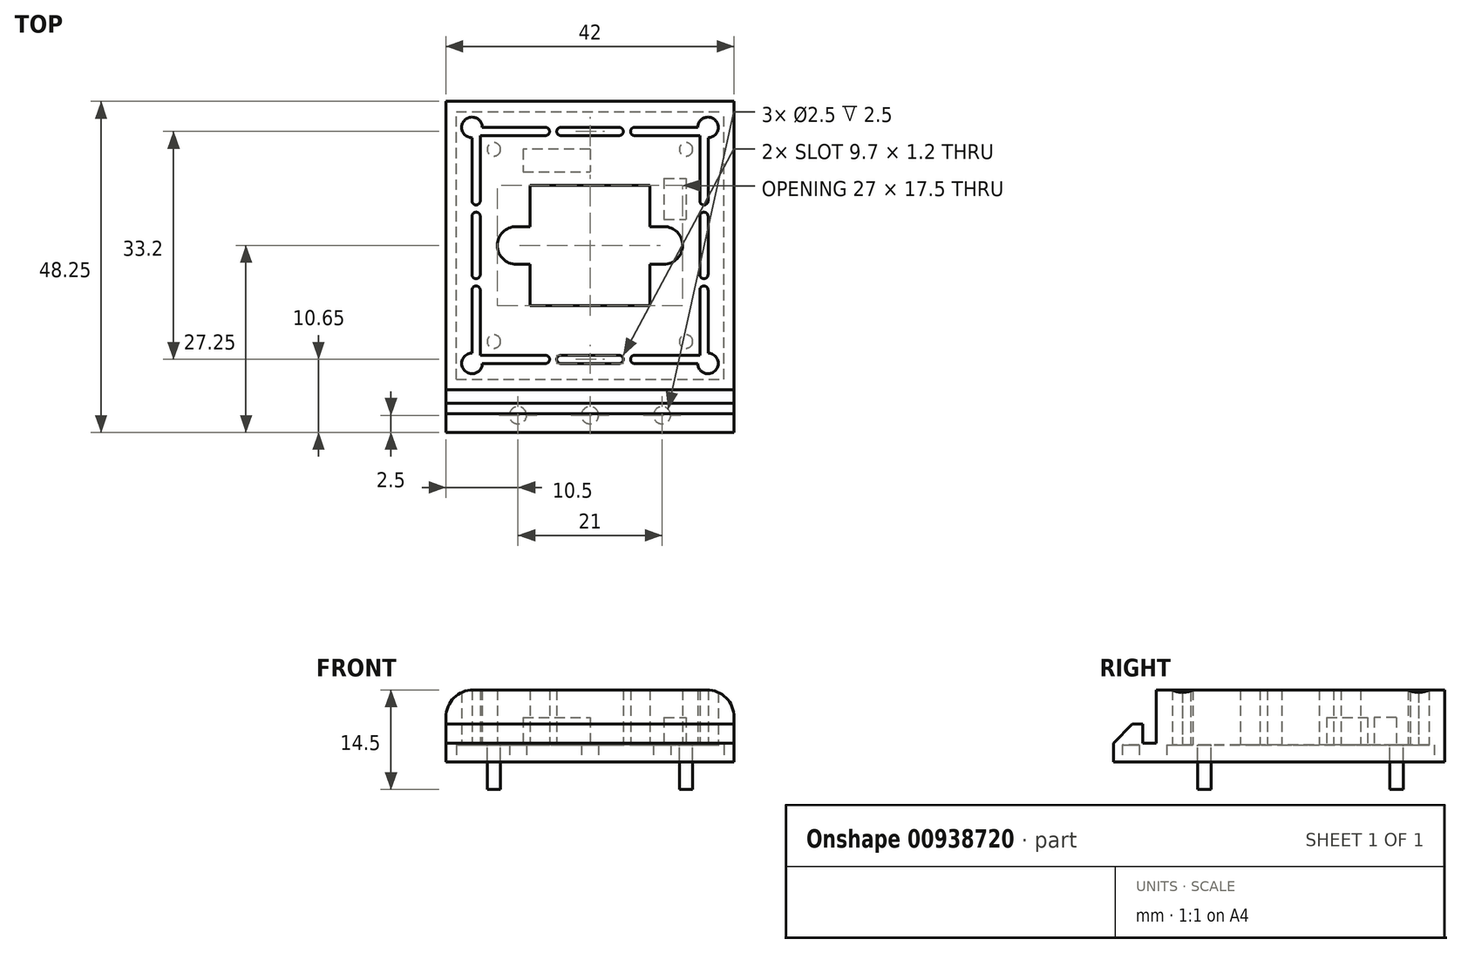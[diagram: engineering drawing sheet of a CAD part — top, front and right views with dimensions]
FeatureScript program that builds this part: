
annotation { "Feature Type Name" : "Feature", "Feature Type Description" : "" }
export const myFeature = defineFeature(function(context is Context, id is Id, definition is map)
    precondition{}
    {
        {
            var Q0;
            Q0=qCreatedBy(makeId("Top.planeOp"),FACE);
            var sketch = newSketch(context, id + "F0", { "sketchPlane" : qUnion([Q0])});
            skLineSegment(sketch, "E0.bottom", {"start": v(19, 19) * mm, "end": v(-19, 19) * mm, "construction": true});
            skLineSegment(sketch, "E0.top", {"start": v(19, -19) * mm, "end": v(-19, -19) * mm, "construction": true});
            skLineSegment(sketch, "E0.left", {"start": v(19, 19) * mm, "end": v(19, -19) * mm, "construction": true});
            skLineSegment(sketch, "E0.right", {"start": v(-19, 19) * mm, "end": v(-19, -19) * mm, "construction": true});
            skPoint(sketch, "E0.middle", {"position": v(0, 0) * mm});
            skPoint(sketch, "E1", {"position": v(19, 0) * mm});
            skPoint(sketch, "E2", {"position": v(-19, 0) * mm});
            skPoint(sketch, "E3", {"position": v(0, 19) * mm});
            skPoint(sketch, "E4", {"position": v(0, -19) * mm});
            skPoint(sketch, "E5", {"position": v(17.2, 0) * mm});
            skPoint(sketch, "E6", {"position": v(-17.2, 0) * mm});
            skLineSegment(sketch, "E7", {"start": v(-19, 0) * mm, "end": v(-17.2, 0) * mm, "construction": true});
            skLineSegment(sketch, "E8", {"start": v(19, 0) * mm, "end": v(17.2, 0) * mm, "construction": true});
            skLineSegment(sketch, "E9", {"start": v(0, 19) * mm, "end": v(0, 17.2) * mm, "construction": true});
            skLineSegment(sketch, "E10", {"start": v(0, -17.2) * mm, "end": v(0, -19) * mm, "construction": true});
            skPoint(sketch, "E11", {"position": v(-16, 16) * mm});
            skPoint(sketch, "E12", {"position": v(16, -16) * mm});
            skPoint(sketch, "E13", {"position": v(16, 16) * mm});
            skPoint(sketch, "E14", {"position": v(-16, -16) * mm});
            skPoint(sketch, "E15", {"position": v(17.2, 4.25) * mm});
            skPoint(sketch, "E16", {"position": v(17.2, -4.25) * mm});
            skPoint(sketch, "E17", {"position": v(16, -4.25) * mm});
            skPoint(sketch, "E18", {"position": v(16, 4.25) * mm});
            skPoint(sketch, "E19", {"position": v(-17.2, 4.25) * mm});
            skPoint(sketch, "E20", {"position": v(-16, 4.25) * mm});
            skPoint(sketch, "E21", {"position": v(-17.2, -4.25) * mm});
            skPoint(sketch, "E22", {"position": v(-16, -4.25) * mm});
            skPoint(sketch, "E23", {"position": v(-4.25, 17.2) * mm});
            skPoint(sketch, "E24", {"position": v(-4.25, 16) * mm});
            skPoint(sketch, "E25", {"position": v(4.25, 17.2) * mm});
            skPoint(sketch, "E26", {"position": v(4.25, 16) * mm});
            skPoint(sketch, "E27", {"position": v(-4.25, -16) * mm});
            skPoint(sketch, "E28", {"position": v(4.25, -16) * mm});
            skPoint(sketch, "E29", {"position": v(-4.25, -17.2) * mm});
            skPoint(sketch, "E30", {"position": v(4.25, -17.2) * mm});
            skLineSegment(sketch, "E31", {"start": v(17.2, 4.25) * mm, "end": v(17.2, -4.25) * mm});
            skLineSegment(sketch, "E32", {"start": v(16, 4.25) * mm, "end": v(16, -4.25) * mm});
            skLineSegment(sketch, "E33", {"start": v(4.25, 16) * mm, "end": v(-4.25, 16) * mm});
            skLineSegment(sketch, "E34", {"start": v(-4.25, 17.2) * mm, "end": v(4.25, 17.2) * mm});
            skLineSegment(sketch, "E35", {"start": v(-16, 4.25) * mm, "end": v(-16, -4.25) * mm});
            skLineSegment(sketch, "E36", {"start": v(-17.2, -4.25) * mm, "end": v(-17.2, 4.25) * mm});
            skLineSegment(sketch, "E37", {"start": v(-4.25, -16) * mm, "end": v(4.25, -16) * mm});
            skLineSegment(sketch, "E38", {"start": v(4.25, -17.2) * mm, "end": v(-4.25, -17.2) * mm});
            skArc(sketch, "E39", {"start": v(16, 4.25) * mm, "mid": v(16.6, 4.85) * mm, "end": v(17.2, 4.25) * mm});
            skArc(sketch, "E40", {"start": v(17.2, -4.25) * mm, "mid": v(16.6, -4.85) * mm, "end": v(16, -4.25) * mm});
            skArc(sketch, "E41", {"start": v(4.25, -16) * mm, "mid": v(4.85, -16.6) * mm, "end": v(4.25, -17.2) * mm});
            skArc(sketch, "E42", {"start": v(-4.25, -16) * mm, "mid": v(-4.85, -16.6) * mm, "end": v(-4.25, -17.2) * mm});
            skArc(sketch, "E43", {"start": v(-17.2, -4.25) * mm, "mid": v(-16.6, -4.85) * mm, "end": v(-16, -4.25) * mm});
            skArc(sketch, "E44", {"start": v(-17.2, 4.25) * mm, "mid": v(-16.6, 4.85) * mm, "end": v(-16, 4.25) * mm});
            skArc(sketch, "E45", {"start": v(-4.25, 16) * mm, "mid": v(-4.85, 16.6) * mm, "end": v(-4.25, 17.2) * mm});
            skArc(sketch, "E46", {"start": v(4.25, 16) * mm, "mid": v(4.85, 16.6) * mm, "end": v(4.25, 17.2) * mm});
            skPoint(sketch, "E47", {"position": v(-6.5, 16) * mm});
            skPoint(sketch, "E48", {"position": v(-6.5, 17.2) * mm});
            skPoint(sketch, "E49", {"position": v(-16, 6.5) * mm});
            skPoint(sketch, "E50", {"position": v(-17.2, 6.5) * mm});
            skPoint(sketch, "E51", {"position": v(6.5, 16) * mm});
            skPoint(sketch, "E52", {"position": v(6.5, 17.2) * mm});
            skPoint(sketch, "E53", {"position": v(16, 6.5) * mm});
            skPoint(sketch, "E54", {"position": v(17.2, 6.5) * mm});
            skPoint(sketch, "E55", {"position": v(-17.2, -6.5) * mm});
            skPoint(sketch, "E56", {"position": v(-16, -6.5) * mm});
            skPoint(sketch, "E57", {"position": v(17.2, -6.5) * mm});
            skPoint(sketch, "E58", {"position": v(16, -6.5) * mm});
            skPoint(sketch, "E59", {"position": v(6.5, -17.2) * mm});
            skPoint(sketch, "E60", {"position": v(6.5, -16) * mm});
            skPoint(sketch, "E61", {"position": v(-6.5, -17.2) * mm});
            skPoint(sketch, "E62", {"position": v(-6.5, -16) * mm});
            skLineSegment(sketch, "E63", {"start": v(-6.5, 17.2) * mm, "end": v(-6.5, 16) * mm, "construction": true});
            skLineSegment(sketch, "E64", {"start": v(-17.2, 6.5) * mm, "end": v(-16, 6.5) * mm, "construction": true});
            skLineSegment(sketch, "E65", {"start": v(6.5, 17.2) * mm, "end": v(6.5, 16) * mm, "construction": true});
            skLineSegment(sketch, "E66", {"start": v(16, 6.5) * mm, "end": v(17.2, 6.5) * mm, "construction": true});
            skLineSegment(sketch, "E67", {"start": v(-17.2, -6.5) * mm, "end": v(-16, -6.5) * mm, "construction": true});
            skLineSegment(sketch, "E68", {"start": v(-6.5, -16) * mm, "end": v(-6.5, -17.2) * mm, "construction": true});
            skLineSegment(sketch, "E69", {"start": v(16, -6.5) * mm, "end": v(17.2, -6.5) * mm, "construction": true});
            skLineSegment(sketch, "E70", {"start": v(6.5, -16) * mm, "end": v(6.5, -17.2) * mm, "construction": true});
            skArc(sketch, "E71", {"start": v(-6.5, 17.2) * mm, "mid": v(-5.9, 16.6) * mm, "end": v(-6.5, 16) * mm});
            skArc(sketch, "E72", {"start": v(-16, 6.5) * mm, "mid": v(-16.6, 5.9) * mm, "end": v(-17.2, 6.5) * mm});
            skArc(sketch, "E73", {"start": v(6.5, 17.2) * mm, "mid": v(5.9, 16.6) * mm, "end": v(6.5, 16) * mm});
            skArc(sketch, "E74", {"start": v(17.2, 6.5) * mm, "mid": v(16.6, 5.9) * mm, "end": v(16, 6.5) * mm});
            skArc(sketch, "E75", {"start": v(-16, -6.5) * mm, "mid": v(-16.6, -5.9) * mm, "end": v(-17.2, -6.5) * mm});
            skArc(sketch, "E76", {"start": v(-6.5, -16) * mm, "mid": v(-5.9, -16.6) * mm, "end": v(-6.5, -17.2) * mm});
            skArc(sketch, "E77", {"start": v(6.5, -16) * mm, "mid": v(5.9, -16.6) * mm, "end": v(6.5, -17.2) * mm});
            skArc(sketch, "E78", {"start": v(17.2, -6.5) * mm, "mid": v(16.6, -5.9) * mm, "end": v(16, -6.5) * mm});
            skLineSegment(sketch, "E79", {"start": v(6.5, 17.2) * mm, "end": v(16, 17.2) * mm});
            skLineSegment(sketch, "E80", {"start": v(6.5, 16) * mm, "end": v(16, 16) * mm});
            skLineSegment(sketch, "E81", {"start": v(16, 6.5) * mm, "end": v(16, 16) * mm});
            skLineSegment(sketch, "E82", {"start": v(17.2, 16) * mm, "end": v(17.2, 6.5) * mm});
            skLineSegment(sketch, "E83", {"start": v(-16, 17.2) * mm, "end": v(-6.5, 17.2) * mm});
            skLineSegment(sketch, "E84", {"start": v(-16, 16) * mm, "end": v(-6.5, 16) * mm});
            skLineSegment(sketch, "E85", {"start": v(-16, 16) * mm, "end": v(-16, 6.5) * mm});
            skLineSegment(sketch, "E86", {"start": v(-17.2, 6.5) * mm, "end": v(-17.2, 16) * mm});
            skLineSegment(sketch, "E87", {"start": v(-16, -6.5) * mm, "end": v(-16, -16) * mm});
            skLineSegment(sketch, "E88", {"start": v(-6.5, -16) * mm, "end": v(-16, -16) * mm});
            skLineSegment(sketch, "E89", {"start": v(-17.2, -6.5) * mm, "end": v(-17.2, -16) * mm});
            skLineSegment(sketch, "E90", {"start": v(-16, -17.2) * mm, "end": v(-6.5, -17.2) * mm});
            skLineSegment(sketch, "E91", {"start": v(6.5, -17.2) * mm, "end": v(16, -17.2) * mm});
            skLineSegment(sketch, "E92", {"start": v(6.5, -16) * mm, "end": v(16, -16) * mm});
            skLineSegment(sketch, "E93", {"start": v(17.2, -16) * mm, "end": v(17.2, -6.5) * mm});
            skLineSegment(sketch, "E94", {"start": v(16, -6.5) * mm, "end": v(16, -16) * mm});
            skLineSegment(sketch, "E95", {"start": v(-17.2, 6.5) * mm, "end": v(-19, 6.5) * mm, "construction": true});
            skLineSegment(sketch, "E96", {"start": v(-17.2, -6.5) * mm, "end": v(-19, -6.5) * mm, "construction": true});
            skLineSegment(sketch, "E97", {"start": v(-6.5, 17.2) * mm, "end": v(-6.5, 19) * mm, "construction": true});
            skLineSegment(sketch, "E98", {"start": v(-6.5, -17.2) * mm, "end": v(-6.5, -19) * mm, "construction": true});
            skLineSegment(sketch, "E99", {"start": v(6.5, -17.2) * mm, "end": v(6.5, -19) * mm, "construction": true});
            skLineSegment(sketch, "E100", {"start": v(17.2, -6.5) * mm, "end": v(19, -6.5) * mm, "construction": true});
            skLineSegment(sketch, "E101", {"start": v(17.2, 6.5) * mm, "end": v(19, 6.5) * mm, "construction": true});
            skLineSegment(sketch, "E102", {"start": v(6.5, 17.2) * mm, "end": v(6.5, 19) * mm, "construction": true});
            skPoint(sketch, "E103", {"position": v(-11.25, 17.2) * mm});
            skPoint(sketch, "E104", {"position": v(-11.25, 16) * mm});
            skPoint(sketch, "E105", {"position": v(-17.2, 11.25) * mm});
            skPoint(sketch, "E106", {"position": v(-16, 11.25) * mm});
            skPoint(sketch, "E107", {"position": v(11.25, 17.2) * mm});
            skPoint(sketch, "E108", {"position": v(11.25, 16) * mm});
            skPoint(sketch, "E109", {"position": v(16, 11.25) * mm});
            skPoint(sketch, "E110", {"position": v(17.2, 11.25) * mm});
            skPoint(sketch, "E111", {"position": v(16, -11.25) * mm});
            skPoint(sketch, "E112", {"position": v(17.2, -11.25) * mm});
            skPoint(sketch, "E113", {"position": v(11.25, -16) * mm});
            skPoint(sketch, "E114", {"position": v(11.25, -17.2) * mm});
            skPoint(sketch, "E115", {"position": v(-11.25, -16) * mm});
            skPoint(sketch, "E116", {"position": v(-11.25, -17.2) * mm});
            skPoint(sketch, "E117", {"position": v(-16, -11.25) * mm});
            skPoint(sketch, "E118", {"position": v(-17.2, -11.25) * mm});
            skLineSegment(sketch, "E119", {"start": v(-17.2, 11.25) * mm, "end": v(-16, 11.25) * mm, "construction": true});
            skLineSegment(sketch, "E120", {"start": v(-11.25, 17.2) * mm, "end": v(-11.25, 16) * mm, "construction": true});
            skLineSegment(sketch, "E121", {"start": v(-11.25, -16) * mm, "end": v(-11.25, -17.2) * mm, "construction": true});
            skLineSegment(sketch, "E122", {"start": v(-16, -11.25) * mm, "end": v(-17.2, -11.25) * mm, "construction": true});
            skLineSegment(sketch, "E123", {"start": v(11.25, 17.2) * mm, "end": v(11.25, 16) * mm, "construction": true});
            skLineSegment(sketch, "E124", {"start": v(16, 11.25) * mm, "end": v(17.2, 11.25) * mm, "construction": true});
            skLineSegment(sketch, "E125", {"start": v(11.25, -17.2) * mm, "end": v(11.25, -16) * mm, "construction": true});
            skLineSegment(sketch, "E126", {"start": v(16, -11.25) * mm, "end": v(17.2, -11.25) * mm, "construction": true});
            skPoint(sketch, "E127", {"position": v(-14, 14) * mm});
            skLineSegment(sketch, "E128", {"start": v(-14, 19) * mm, "end": v(-14, 14) * mm, "construction": true});
            skLineSegment(sketch, "E129", {"start": v(-14, 14) * mm, "end": v(-19, 14) * mm, "construction": true});
            skPoint(sketch, "E130", {"position": v(-14, -14) * mm});
            skLineSegment(sketch, "E131", {"start": v(-19, -14) * mm, "end": v(-14, -14) * mm, "construction": true});
            skLineSegment(sketch, "E132", {"start": v(-14, -19) * mm, "end": v(-14, -14) * mm, "construction": true});
            skPoint(sketch, "E133", {"position": v(14, -14) * mm});
            skLineSegment(sketch, "E134", {"start": v(14, -19) * mm, "end": v(14, -14) * mm, "construction": true});
            skLineSegment(sketch, "E135", {"start": v(14, -14) * mm, "end": v(19, -14) * mm, "construction": true});
            skPoint(sketch, "E136", {"position": v(14, 14) * mm});
            skLineSegment(sketch, "E137", {"start": v(14, 19) * mm, "end": v(14, 14) * mm, "construction": true});
            skLineSegment(sketch, "E138", {"start": v(19, 14) * mm, "end": v(14, 14) * mm, "construction": true});
            skPoint(sketch, "E139", {"position": v(16, 0) * mm});
            skPoint(sketch, "E140", {"position": v(0, 16) * mm});
            skPoint(sketch, "E141", {"position": v(-16, 0) * mm});
            skPoint(sketch, "E142", {"position": v(0, -16) * mm});
            skLineSegment(sketch, "E143", {"start": v(16, 0) * mm, "end": v(17.2, 0) * mm, "construction": true});
            skLineSegment(sketch, "E144", {"start": v(0, 17.2) * mm, "end": v(0, 16) * mm, "construction": true});
            skLineSegment(sketch, "E145", {"start": v(0, -16) * mm, "end": v(0, -17.2) * mm, "construction": true});
            skLineSegment(sketch, "E146", {"start": v(-17.2, 0) * mm, "end": v(-16, 0) * mm, "construction": true});
            skPoint(sketch, "E147", {"position": v(-17.2, 17.2) * mm});
            skPoint(sketch, "E148", {"position": v(17.2, 17.2) * mm});
            skPoint(sketch, "E149", {"position": v(-17.2, -17.2) * mm});
            skPoint(sketch, "E150", {"position": v(17.2, -17.2) * mm});
            skLineSegment(sketch, "E151", {"start": v(16, 4.25) * mm, "end": v(17.2, 4.25) * mm, "construction": true});
            skLineSegment(sketch, "E152", {"start": v(16, -4.25) * mm, "end": v(17.2, -4.25) * mm, "construction": true});
            skLineSegment(sketch, "E153", {"start": v(-4.25, 16) * mm, "end": v(-4.25, 17.2) * mm, "construction": true});
            skLineSegment(sketch, "E154", {"start": v(4.25, 16) * mm, "end": v(4.25, 17.2) * mm, "construction": true});
            skLineSegment(sketch, "E155", {"start": v(-16, 4.25) * mm, "end": v(-17.2, 4.25) * mm, "construction": true});
            skLineSegment(sketch, "E156", {"start": v(-16, -4.25) * mm, "end": v(-17.2, -4.25) * mm, "construction": true});
            skLineSegment(sketch, "E157", {"start": v(-4.25, -16) * mm, "end": v(-4.25, -17.2) * mm, "construction": true});
            skLineSegment(sketch, "E158", {"start": v(4.25, -16) * mm, "end": v(4.25, -17.2) * mm, "construction": true});
            skLineSegment(sketch, "E159", {"start": v(-6.5, 17.2) * mm, "end": v(-4.25, 17.2) * mm, "construction": true});
            skLineSegment(sketch, "E160", {"start": v(4.25, 17.2) * mm, "end": v(6.5, 17.2) * mm, "construction": true});
            skLineSegment(sketch, "E161", {"start": v(17.2, 6.5) * mm, "end": v(17.2, 4.25) * mm, "construction": true});
            skLineSegment(sketch, "E162", {"start": v(17.2, -6.5) * mm, "end": v(17.2, -4.25) * mm, "construction": true});
            skLineSegment(sketch, "E163", {"start": v(6.5, -17.2) * mm, "end": v(4.25, -17.2) * mm, "construction": true});
            skLineSegment(sketch, "E164", {"start": v(-4.25, -17.2) * mm, "end": v(-6.5, -17.2) * mm, "construction": true});
            skLineSegment(sketch, "E165", {"start": v(-17.2, -6.5) * mm, "end": v(-17.2, -4.25) * mm, "construction": true});
            skLineSegment(sketch, "E166", {"start": v(-17.2, 4.25) * mm, "end": v(-17.2, 6.5) * mm, "construction": true});
            skCircle(sketch, "E167", {"center": v(14, 14) * mm, "radius": 0.97 * mm});
            skPoint(sketch, "E168", {"position": v(14, 14.97) * mm});
            skPoint(sketch, "E169", {"position": v(14.97, 14) * mm});
            skPoint(sketch, "E170", {"position": v(16, 14) * mm});
            skPoint(sketch, "E171", {"position": v(14, 16) * mm});
            skCircle(sketch, "E172", {"center": v(-14, 14) * mm, "radius": 0.97 * mm});
            skPoint(sketch, "E173", {"position": v(-14, 14.97) * mm});
            skPoint(sketch, "E174", {"position": v(-14.97, 14) * mm});
            skCircle(sketch, "E175", {"center": v(-14, -14) * mm, "radius": 0.97 * mm});
            skCircle(sketch, "E176", {"center": v(14, -14) * mm, "radius": 0.97 * mm});
            skPoint(sketch, "E177", {"position": v(14, -14.97) * mm});
            skPoint(sketch, "E178", {"position": v(14.97, -14) * mm});
            skPoint(sketch, "E179", {"position": v(-14.97, -14) * mm});
            skPoint(sketch, "E180", {"position": v(-14, -14.97) * mm});
            skLineSegment(sketch, "E181.bottom", {"start": v(8.75, 8.75) * mm, "end": v(-8.75, 8.75) * mm});
            skLineSegment(sketch, "E181.top", {"start": v(8.75, -8.75) * mm, "end": v(-8.75, -8.75) * mm});
            skLineSegment(sketch, "E181.left", {"start": v(8.75, 8.75) * mm, "end": v(8.75, 2.75) * mm});
            skLineSegment(sketch, "E181.right", {"start": v(-8.75, 8.75) * mm, "end": v(-8.75, 2.75) * mm});
            skLineSegment(sketch, "E182.bottom", {"start": v(-21, 21) * mm, "end": v(-2.62, 21) * mm});
            skLineSegment(sketch, "E182.top", {"start": v(-21, -21) * mm, "end": v(-2.63, -21) * mm});
            skLineSegment(sketch, "E182.left", {"start": v(-21, 21) * mm, "end": v(-21, -21) * mm});
            skLineSegment(sketch, "E182.right", {"start": v(21, 21) * mm, "end": v(21, -21) * mm});
            skPoint(sketch, "E183", {"position": v(0, 21) * mm});
            skPoint(sketch, "E184", {"position": v(-2.62, 21) * mm});
            skPoint(sketch, "E185", {"position": v(2.62, 21) * mm});
            skLineSegment(sketch, "E186.trimOffspring", {"start": v(2.62, 21) * mm, "end": v(21, 21) * mm});
            skPoint(sketch, "E187", {"position": v(0, -21) * mm});
            skPoint(sketch, "E188", {"position": v(-2.63, -21) * mm});
            skPoint(sketch, "E189", {"position": v(2.63, -21) * mm});
            skLineSegment(sketch, "E190.trimOffspring", {"start": v(2.63, -21) * mm, "end": v(21, -21) * mm});
            skLineSegment(sketch, "E191", {"start": v(-2.62, 21) * mm, "end": v(2.63, 21) * mm});
            skLineSegment(sketch, "E192", {"start": v(-2.63, -21) * mm, "end": v(2.63, -21) * mm});
            skPoint(sketch, "E193", {"position": v(-8.75, 0) * mm});
            skPoint(sketch, "E194", {"position": v(8.75, 0) * mm});
            skPoint(sketch, "E195", {"position": v(8.75, -2.75) * mm});
            skPoint(sketch, "E196", {"position": v(8.75, 2.75) * mm});
            skPoint(sketch, "E197", {"position": v(-8.75, -2.75) * mm});
            skPoint(sketch, "E198", {"position": v(-8.75, 2.75) * mm});
            skLineSegment(sketch, "E199", {"start": v(-8.75, -2.75) * mm, "end": v(8.75, -2.75) * mm, "construction": true});
            skLineSegment(sketch, "E200", {"start": v(8.75, 2.75) * mm, "end": v(-8.75, 2.75) * mm, "construction": true});
            skPoint(sketch, "E201", {"position": v(10.75, 0) * mm});
            skPoint(sketch, "E202", {"position": v(-10.75, 0) * mm});
            skLineSegment(sketch, "E203", {"start": v(10.75, 0) * mm, "end": v(8.75, 0) * mm, "construction": true});
            skLineSegment(sketch, "E204", {"start": v(-10.75, 0) * mm, "end": v(-8.75, 0) * mm, "construction": true});
            skLineSegment(sketch, "E205", {"start": v(-8.75, -2.75) * mm, "end": v(-10.75, -2.75) * mm});
            skLineSegment(sketch, "E206", {"start": v(-8.75, 2.75) * mm, "end": v(-10.75, 2.75) * mm});
            skLineSegment(sketch, "E207", {"start": v(8.75, -2.75) * mm, "end": v(10.75, -2.75) * mm});
            skLineSegment(sketch, "E208", {"start": v(8.75, 2.75) * mm, "end": v(10.75, 2.75) * mm});
            skArc(sketch, "E209", {"start": v(-10.75, 2.75) * mm, "mid": v(-13.5, 0) * mm, "end": v(-10.75, -2.75) * mm});
            skArc(sketch, "E210", {"start": v(10.75, -2.75) * mm, "mid": v(13.5, 0) * mm, "end": v(10.75, 2.75) * mm});
            skLineSegment(sketch, "E211.trimOffspring", {"start": v(-8.75, -2.75) * mm, "end": v(-8.75, -8.75) * mm});
            skLineSegment(sketch, "E212.trimOffspring", {"start": v(8.75, -2.75) * mm, "end": v(8.75, -8.75) * mm});
            skLineSegment(sketch, "E213", {"start": v(-16, -6.5) * mm, "end": v(-16, -4.25) * mm});
            skLineSegment(sketch, "E214", {"start": v(-16, 4.25) * mm, "end": v(-16, 6.5) * mm});
            skLineSegment(sketch, "E215", {"start": v(-6.5, -16) * mm, "end": v(-4.25, -16) * mm});
            skLineSegment(sketch, "E216", {"start": v(4.25, -16) * mm, "end": v(6.5, -16) * mm});
            skLineSegment(sketch, "E217", {"start": v(16, -4.25) * mm, "end": v(16, -6.5) * mm});
            skLineSegment(sketch, "E218", {"start": v(16, 4.25) * mm, "end": v(16, 6.5) * mm});
            skLineSegment(sketch, "E219", {"start": v(6.5, 16) * mm, "end": v(4.25, 16) * mm});
            skLineSegment(sketch, "E220", {"start": v(-4.25, 16) * mm, "end": v(-6.5, 16) * mm});
            skArc(sketch, "E221", {"start": v(-15.7, 17.2) * mm, "mid": v(-18.26, 18.26) * mm, "end": v(-17.2, 15.7) * mm});
            skLineSegment(sketch, "E222", {"start": v(-17.2, 16) * mm, "end": v(-17.2, 17.2) * mm, "construction": true});
            skLineSegment(sketch, "E223", {"start": v(-17.2, 17.2) * mm, "end": v(-17.2, 19) * mm, "construction": true});
            skLineSegment(sketch, "E224", {"start": v(-16, 17.2) * mm, "end": v(-17.2, 17.2) * mm, "construction": true});
            skLineSegment(sketch, "E225", {"start": v(-17.2, 17.2) * mm, "end": v(-19, 17.2) * mm, "construction": true});
            skArc(sketch, "E226", {"start": v(17.2, 15.7) * mm, "mid": v(18.26, 18.26) * mm, "end": v(15.7, 17.2) * mm});
            skLineSegment(sketch, "E227", {"start": v(16, 17.2) * mm, "end": v(17.2, 17.2) * mm, "construction": true});
            skLineSegment(sketch, "E228", {"start": v(17.2, 16) * mm, "end": v(17.2, 17.2) * mm, "construction": true});
            skLineSegment(sketch, "E229", {"start": v(17.2, 17.2) * mm, "end": v(17.2, 19) * mm, "construction": true});
            skLineSegment(sketch, "E230", {"start": v(17.2, 17.2) * mm, "end": v(19, 17.2) * mm, "construction": true});
            skArc(sketch, "E231", {"start": v(-17.2, -15.7) * mm, "mid": v(-18.26, -18.26) * mm, "end": v(-15.7, -17.2) * mm});
            skArc(sketch, "E232", {"start": v(15.7, -17.2) * mm, "mid": v(18.26, -18.26) * mm, "end": v(17.2, -15.7) * mm});
            skLineSegment(sketch, "E233", {"start": v(17.2, -16) * mm, "end": v(17.2, -17.2) * mm, "construction": true});
            skLineSegment(sketch, "E234", {"start": v(17.2, -17.2) * mm, "end": v(17.2, -19) * mm, "construction": true});
            skLineSegment(sketch, "E235", {"start": v(16, -17.2) * mm, "end": v(17.2, -17.2) * mm, "construction": true});
            skLineSegment(sketch, "E236", {"start": v(17.2, -17.2) * mm, "end": v(19, -17.2) * mm, "construction": true});
            skLineSegment(sketch, "E237", {"start": v(-17.2, -16) * mm, "end": v(-17.2, -17.2) * mm, "construction": true});
            skLineSegment(sketch, "E238", {"start": v(-17.2, -17.2) * mm, "end": v(-17.2, -19) * mm, "construction": true});
            skLineSegment(sketch, "E239", {"start": v(-16, -17.2) * mm, "end": v(-17.2, -17.2) * mm, "construction": true});
            skLineSegment(sketch, "E240", {"start": v(-17.2, -17.2) * mm, "end": v(-19, -17.2) * mm, "construction": true});
            skPoint(sketch, "E241", {"position": v(15.7, 17.2) * mm});
            skPoint(sketch, "E242", {"position": v(17.2, 15.7) * mm});
            skPoint(sketch, "E243", {"position": v(-17.2, 15.7) * mm});
            skPoint(sketch, "E244", {"position": v(-15.7, 17.2) * mm});
            skPoint(sketch, "E245", {"position": v(-17.2, -15.7) * mm});
            skPoint(sketch, "E246", {"position": v(-15.7, -17.2) * mm});
            skPoint(sketch, "E247", {"position": v(15.7, -17.2) * mm});
            skPoint(sketch, "E248", {"position": v(17.2, -15.7) * mm});
            skLineSegment(sketch, "E249.bottom", {"start": v(-19.5, -19.5) * mm, "end": v(19.5, -19.5) * mm});
            skLineSegment(sketch, "E249.top", {"start": v(-19.5, 19.5) * mm, "end": v(19.5, 19.5) * mm});
            skLineSegment(sketch, "E249.left", {"start": v(-19.5, -19.5) * mm, "end": v(-19.5, 19.5) * mm});
            skLineSegment(sketch, "E249.right", {"start": v(19.5, -19.5) * mm, "end": v(19.5, 19.5) * mm});
            skPoint(sketch, "E250", {"position": v(-8.75, 10.75) * mm});
            skPoint(sketch, "E251", {"position": v(-8.75, 14) * mm});
            skPoint(sketch, "E252", {"position": v(0, 8.75) * mm});
            skPoint(sketch, "E253", {"position": v(0, 10.75) * mm});
            skPoint(sketch, "E254", {"position": v(0, 14) * mm});
            skLineSegment(sketch, "E255", {"start": v(0, 14) * mm, "end": v(0, 10.75) * mm});
            skLineSegment(sketch, "E256", {"start": v(-8.75, 10.75) * mm, "end": v(0, 10.75) * mm});
            skLineSegment(sketch, "E257", {"start": v(0, 14) * mm, "end": v(-8.75, 14) * mm});
            skLineSegment(sketch, "E258", {"start": v(-8.75, 14) * mm, "end": v(-9.75, 14) * mm});
            skLineSegment(sketch, "E259", {"start": v(-9.75, 14) * mm, "end": v(-9.75, 10.75) * mm});
            skLineSegment(sketch, "E260", {"start": v(-9.75, 10.75) * mm, "end": v(-8.75, 10.75) * mm});
            skPoint(sketch, "E261", {"position": v(10.75, 8.75) * mm});
            skPoint(sketch, "E262", {"position": v(14, 8.75) * mm});
            skLineSegment(sketch, "E263", {"start": v(10.75, 8.75) * mm, "end": v(10.75, 3.81) * mm});
            skLineSegment(sketch, "E264", {"start": v(10.75, 3.81) * mm, "end": v(14, 3.81) * mm});
            skLineSegment(sketch, "E265", {"start": v(14, 3.81) * mm, "end": v(14, 8.75) * mm});
            skLineSegment(sketch, "E266", {"start": v(10.75, 8.75) * mm, "end": v(10.75, 9.75) * mm});
            skLineSegment(sketch, "E267", {"start": v(10.75, 9.75) * mm, "end": v(14, 9.75) * mm});
            skLineSegment(sketch, "E268", {"start": v(14, 9.75) * mm, "end": v(14, 8.75) * mm});
            skSolve(sketch);
        }
        {
            var Q0;
            Q0 = qSketchRegion(id + "F0", true);
            var Q1;
            Q1=makeQuery(id+"F0.imprint","IMPRINT",FACE,{"disambiguationData":[TD([[makeQuery(id+"F0.imprint","IMPRINT",EDGE,{"derivedFrom":sQuery(id+"F0.wireOp",EDGE,"E176")}),1.0]])]});
            var Q2;
            Q2=makeQuery(id+"F0.imprint","IMPRINT",FACE,{"disambiguationData":[TD([[makeQuery(id+"F0.imprint","IMPRINT",EDGE,{"derivedFrom":sQuery(id+"F0.wireOp",EDGE,"E175")}),1.0]])]});
            var Q3;
            Q3=makeQuery(id+"F0.imprint","IMPRINT",FACE,{"disambiguationData":[TD([[makeQuery(id+"F0.imprint","IMPRINT",EDGE,{"derivedFrom":sQuery(id+"F0.wireOp",EDGE,"E172")}),1.0]])]});
            var Q4;
            Q4=makeQuery(id+"F0.imprint","IMPRINT",FACE,{"disambiguationData":[TD([[makeQuery(id+"F0.imprint","IMPRINT",EDGE,{"derivedFrom":sQuery(id+"F0.wireOp",EDGE,"E167")}),1.0]])]});
            var Q5;
            Q5=makeQuery(id+"F0.imprint","IMPRINT",FACE,{"disambiguationData":[TD([[makeQuery(id+"F0.imprint","IMPRINT",EDGE,{"derivedFrom":sQuery(id+"F0.wireOp",EDGE,"E32")}),-1.0]])]});
            var Q6;
            Q6=makeQuery(id+"F0.imprint","IMPRINT",FACE,{"disambiguationData":[TD([[makeQuery(id+"F0.imprint","IMPRINT",EDGE,{"derivedFrom":sQuery(id+"F0.wireOp",EDGE,"E31")}),1.0]])]});
            var Q7;
            Q7=makeQuery(id+"F0.imprint","IMPRINT",FACE,{"disambiguationData":[TD([[makeQuery(id+"F0.imprint","IMPRINT",EDGE,{"derivedFrom":sQuery(id+"F0.wireOp",EDGE,"E263")}),1.0]])]});
            var Q8;
            Q8=makeQuery(id+"F0.imprint","IMPRINT",FACE,{"disambiguationData":[TD([[makeQuery(id+"F0.imprint","IMPRINT",EDGE,{"derivedFrom":sQuery(id+"F0.wireOp",EDGE,"E255")}),-1.0]])]});
            extrude(context, id + "F1", {"entities" : qUnion([Q0, Q1, Q2, Q3, Q4, Q5, Q6, Q7, Q8]), "depth" : 9 * mm, "offsetDistance" : 25 * mm});
        }
        {
            var Q0;
            Q0=makeQuery(id+"F1.opExtrude","CAP_EDGE",EDGE,{"disambiguationData":[OSD([sQuery(id+"F0.wireOp",EDGE,"E182.left")])],"isStart":false});
            var Q1;
            Q1=makeQuery(id+"F1.opExtrude","CAP_EDGE",EDGE,{"disambiguationData":[OSD([sQuery(id+"F0.wireOp",EDGE,"E182.right")])],"isStart":false});
            fillet(context, id + "F2", {"entities" : qUnion([Q0, Q1]), "radius" : 4 * mm, "tangentPropagation" : true, "allowEdgeOverflow" : false});
        }
        {
            var Q0;
            Q0=qCreatedBy(makeId("Right.planeOp"),FACE);
            var sketch = newSketch(context, id + "F3", { "sketchPlane" : qUnion([Q0])});
            skLineSegment(sketch, "E269", {"start": v(-21, 1.25) * mm, "end": v(-21, 0) * mm});
            skLineSegment(sketch, "E270", {"start": v(-21, 0) * mm, "end": v(-21, -1.5) * mm});
            skLineSegment(sketch, "E271", {"start": v(-21, -1.5) * mm, "end": v(-23, -1.5) * mm});
            skLineSegment(sketch, "E272", {"start": v(-21, 1.25) * mm, "end": v(-23, 1.25) * mm});
            skLineSegment(sketch, "E273", {"start": v(-23, 1.25) * mm, "end": v(-23, -1.5) * mm, "construction": true});
            skLineSegment(sketch, "E274", {"start": v(-23, 1.25) * mm, "end": v(-23, 4) * mm});
            skLineSegment(sketch, "E275", {"start": v(-23, 4) * mm, "end": v(-24.5, 4) * mm});
            skLineSegment(sketch, "E276", {"start": v(-24.5, 4) * mm, "end": v(-27.25, 1.25) * mm});
            skLineSegment(sketch, "E277", {"start": v(-27.25, 1.25) * mm, "end": v(-27.25, -1.5) * mm});
            skLineSegment(sketch, "E278", {"start": v(-27.25, -1.5) * mm, "end": v(-23, -1.5) * mm});
            skSolve(sketch);
        }
        {
            var Q0;
            Q0 = qSketchRegion(id + "F3", true);
            extrude(context, id + "F4", {"entities" : qUnion([Q0]), "operationType" : NewBodyOperationType.ADD, "depth" : 21 * mm, "offsetDistance" : 25 * mm});
        }
        {
            var Q0;
            Q0=makeQuery(id+"F4.opExtrude","CAP_FACE",FACE,{"disambiguationData":[OSD([sQuery(id+"F3.wireOp",EDGE,"W3A2iIaU-WZcM-LwCZ-avBC-8jkScGPnRnPX"),sQuery(id+"F3.wireOp",EDGE,"ALWewPtL-lRdy-D1S6-Pmp3-0LCmG40DPnmF"),sQuery(id+"F3.wireOp",EDGE,"E269"),sQuery(id+"F3.wireOp",EDGE,"a8HGcZms-0psD-ubHa-zhNr-YMWZytVFjQNi"),sQuery(id+"F3.wireOp",EDGE,"o8Ebxgyn-Q84Y-cI0J-CGKw-LX74F4kokC7l"),sQuery(id+"F3.wireOp",EDGE,"YJE5rnin-kTqy-YI2g-DbKN-iJDOnxPtUyyk"),sQuery(id+"F3.wireOp",EDGE,"J2bwKcV5-MZwX-Vs9f-UurF-KyFTJAMSioa0"),sQuery(id+"F3.wireOp",EDGE,"OojeKQKz-hSKq-U6jK-n3HU-CNnbXeyMiDCb")])],"isStart":true});
            extrude(context, id + "F5", {"entities" : qUnion([Q0]), "operationType" : NewBodyOperationType.ADD, "depth" : 21 * mm, "offsetDistance" : 25 * mm});
        }
        {
            var Q0;
            Q0=makeQuery(id+"F0.imprint","IMPRINT",FACE,{"disambiguationData":[TD([[makeQuery(id+"F0.imprint","IMPRINT",EDGE,{"derivedFrom":sQuery(id+"F0.wireOp",EDGE,"E175")}),1.0]])]});
            var Q1;
            Q1=makeQuery(id+"F0.imprint","IMPRINT",FACE,{"disambiguationData":[TD([[makeQuery(id+"F0.imprint","IMPRINT",EDGE,{"derivedFrom":sQuery(id+"F0.wireOp",EDGE,"E176")}),1.0]])]});
            var Q2;
            Q2=makeQuery(id+"F0.imprint","IMPRINT",FACE,{"disambiguationData":[TD([[makeQuery(id+"F0.imprint","IMPRINT",EDGE,{"derivedFrom":sQuery(id+"F0.wireOp",EDGE,"E172")}),1.0]])]});
            var Q3;
            Q3=makeQuery(id+"F0.imprint","IMPRINT",FACE,{"disambiguationData":[TD([[makeQuery(id+"F0.imprint","IMPRINT",EDGE,{"derivedFrom":sQuery(id+"F0.wireOp",EDGE,"E167")}),1.0]])]});
            var Q4;
            Q4=sQuery(id+"F0.wireOp",EDGE,"E175");
            var Q5;
            Q5=sQuery(id+"F0.wireOp",EDGE,"E176");
            var Q6;
            Q6=sQuery(id+"F0.wireOp",EDGE,"E167");
            var Q7;
            Q7=sQuery(id+"F0.wireOp",EDGE,"E172");
            extrude(context, id + "F6", {"entities" : qUnion([Q0, Q1, Q2, Q3]), "operationType" : NewBodyOperationType.ADD, "surfaceEntities" : qUnion([Q4, Q5, Q6, Q7]), "oppositeDirection" : true, "depth" : 5.5 * mm, "offsetDistance" : 25 * mm});
        }
        {
            var Q0;
            Q0=makeQuery(id+"F0.imprint","IMPRINT",FACE,{"disambiguationData":[TD([[makeQuery(id+"F0.imprint","IMPRINT",EDGE,{"derivedFrom":sQuery(id+"F0.wireOp",EDGE,"E31")}),1.0]])]});
            extrude(context, id + "F7", {"entities" : qUnion([Q0]), "operationType" : NewBodyOperationType.ADD, "oppositeDirection" : true, "depth" : 1.5 * mm, "offsetDistance" : 25 * mm});
        }
        {
            var Q0;
            Q0=makeQuery(id+"F7.opExtrude","CAP_FACE",FACE,{"disambiguationData":[OSD([sQuery(id+"F0.wireOp",EDGE,"E31"),sQuery(id+"F0.wireOp",EDGE,"E34"),sQuery(id+"F0.wireOp",EDGE,"E36"),sQuery(id+"F0.wireOp",EDGE,"E38"),sQuery(id+"F0.wireOp",EDGE,"E39"),sQuery(id+"F0.wireOp",EDGE,"E40"),sQuery(id+"F0.wireOp",EDGE,"E41"),sQuery(id+"F0.wireOp",EDGE,"E42"),sQuery(id+"F0.wireOp",EDGE,"E43"),sQuery(id+"F0.wireOp",EDGE,"E44"),sQuery(id+"F0.wireOp",EDGE,"E45"),sQuery(id+"F0.wireOp",EDGE,"E46"),sQuery(id+"F0.wireOp",EDGE,"E71"),sQuery(id+"F0.wireOp",EDGE,"E72"),sQuery(id+"F0.wireOp",EDGE,"E73"),sQuery(id+"F0.wireOp",EDGE,"E74"),sQuery(id+"F0.wireOp",EDGE,"E75"),sQuery(id+"F0.wireOp",EDGE,"E76"),sQuery(id+"F0.wireOp",EDGE,"E77"),sQuery(id+"F0.wireOp",EDGE,"E78"),sQuery(id+"F0.wireOp",EDGE,"E79"),sQuery(id+"F0.wireOp",EDGE,"E82"),sQuery(id+"F0.wireOp",EDGE,"E83"),sQuery(id+"F0.wireOp",EDGE,"E86"),sQuery(id+"F0.wireOp",EDGE,"E89"),sQuery(id+"F0.wireOp",EDGE,"E90"),sQuery(id+"F0.wireOp",EDGE,"E91"),sQuery(id+"F0.wireOp",EDGE,"E93"),sQuery(id+"F0.wireOp",EDGE,"E213"),sQuery(id+"F0.wireOp",EDGE,"E214"),sQuery(id+"F0.wireOp",EDGE,"E215"),sQuery(id+"F0.wireOp",EDGE,"E216"),sQuery(id+"F0.wireOp",EDGE,"E217"),sQuery(id+"F0.wireOp",EDGE,"E218"),sQuery(id+"F0.wireOp",EDGE,"E219"),sQuery(id+"F0.wireOp",EDGE,"E220"),sQuery(id+"F0.wireOp",EDGE,"E221"),sQuery(id+"F0.wireOp",EDGE,"E226"),sQuery(id+"F0.wireOp",EDGE,"E231"),sQuery(id+"F0.wireOp",EDGE,"E232"),sQuery(id+"F0.wireOp",EDGE,"E249.bottom"),sQuery(id+"F0.wireOp",EDGE,"E249.top"),sQuery(id+"F0.wireOp",EDGE,"E249.left"),sQuery(id+"F0.wireOp",EDGE,"E249.right")])],"isStart":false});
            extrude(context, id + "F8", {"entities" : qUnion([Q0]), "operationType" : NewBodyOperationType.REMOVE, "oppositeDirection" : true, "depth" : 2.5 * mm, "offsetDistance" : 25 * mm});
        }
        {
            var Q0;
            Q0=makeQuery(id+"F0.imprint","IMPRINT",FACE,{"disambiguationData":[TD([[makeQuery(id+"F0.imprint","IMPRINT",EDGE,{"derivedFrom":sQuery(id+"F0.wireOp",EDGE,"E182.bottom")}),-1.0]])]});
            extrude(context, id + "F9", {"entities" : qUnion([Q0]), "operationType" : NewBodyOperationType.ADD, "oppositeDirection" : true, "depth" : 1.5 * mm, "offsetDistance" : 25 * mm});
        }
        {
            var Q0;
            {var subQ0=sQuery(id+"F3.wireOp",EDGE,"E278");var subQ1=sQuery(id+"F3.wireOp",EDGE,"E271");Q0=makeQuery(id+"F9.boolean.opBoolean","MERGE",FACE,{"derivedFrom":[makeQuery(id+"F5.boolean.opBoolean","MERGE",FACE,{"derivedFrom":[makeQuery(id+"F4.opExtrude","SWEPT_FACE",FACE,{"disambiguationData":[OSD([subQ1,subQ0])]}),makeQuery(id+"F5.opExtrude","SWEPT_FACE",FACE,{"disambiguationData":[OSD([subQ1,subQ0])]})]}),makeQuery(id+"F9.opExtrude","CAP_FACE",FACE,{"disambiguationData":[OSD([sQuery(id+"F0.wireOp",EDGE,"E182.bottom"),sQuery(id+"F0.wireOp",EDGE,"E182.top"),sQuery(id+"F0.wireOp",EDGE,"E182.left"),sQuery(id+"F0.wireOp",EDGE,"E182.right"),sQuery(id+"F0.wireOp",EDGE,"E186.trimOffspring"),sQuery(id+"F0.wireOp",EDGE,"E190.trimOffspring"),sQuery(id+"F0.wireOp",EDGE,"E191"),sQuery(id+"F0.wireOp",EDGE,"E192"),sQuery(id+"F0.wireOp",EDGE,"E249.bottom"),sQuery(id+"F0.wireOp",EDGE,"E249.top"),sQuery(id+"F0.wireOp",EDGE,"E249.left"),sQuery(id+"F0.wireOp",EDGE,"E249.right")])],"isStart":false})]});}
            var sketch = newSketch(context, id + "F10", { "sketchPlane" : qUnion([Q0])});
            skPoint(sketch, "E279", {"position": v(0, 19.5) * mm});
            skPoint(sketch, "E280", {"position": v(0, 21) * mm});
            skLineSegment(sketch, "E281", {"start": v(0, 21) * mm, "end": v(21, 21) * mm, "construction": true});
            skLineSegment(sketch, "E282", {"start": v(0, 27.25) * mm, "end": v(0, 26) * mm, "construction": true});
            skPoint(sketch, "E283.orphan", {"position": v(-21, 21) * mm});
            skLineSegment(sketch, "E284", {"start": v(0, 21) * mm, "end": v(-21, 21) * mm, "construction": true});
            skLineSegment(sketch, "E285", {"start": v(-10.5, 21) * mm, "end": v(-10.5, 24.75) * mm, "construction": true});
            skLineSegment(sketch, "E286", {"start": v(10.5, 21) * mm, "end": v(10.5, 24.75) * mm, "construction": true});
            skCircle(sketch, "E287", {"center": v(-10.5, 24.75) * mm, "radius": 1.25 * mm});
            skCircle(sketch, "E288", {"center": v(0, 24.75) * mm, "radius": 1.25 * mm});
            skCircle(sketch, "E289", {"center": v(10.5, 24.75) * mm, "radius": 1.25 * mm});
            skPoint(sketch, "E290", {"position": v(-10.5, 26) * mm});
            skPoint(sketch, "E291", {"position": v(0, 26) * mm});
            skPoint(sketch, "E292", {"position": v(10.5, 26) * mm});
            skLineSegment(sketch, "E293.trimOffspring", {"start": v(-10.5, 26) * mm, "end": v(-10.5, 27.25) * mm, "construction": true});
            skLineSegment(sketch, "E294.trimOffspring", {"start": v(0, 24.75) * mm, "end": v(0, 21) * mm, "construction": true});
            skLineSegment(sketch, "E295.trimOffspring", {"start": v(10.5, 26) * mm, "end": v(10.5, 27.25) * mm, "construction": true});
            skSolve(sketch);
        }
        {
            var Q0;
            Q0=makeQuery(id+"F10.imprint","IMPRINT",FACE,{"disambiguationData":[TD([[makeQuery(id+"F10.imprint","IMPRINT",EDGE,{"derivedFrom":sQuery(id+"F10.wireOp",EDGE,"E289")}),1.0]])]});
            var Q1;
            Q1=makeQuery(id+"F10.imprint","IMPRINT",FACE,{"disambiguationData":[TD([[makeQuery(id+"F10.imprint","IMPRINT",EDGE,{"derivedFrom":sQuery(id+"F10.wireOp",EDGE,"E288")}),1.0]])]});
            var Q2;
            Q2=makeQuery(id+"F10.imprint","IMPRINT",FACE,{"disambiguationData":[TD([[makeQuery(id+"F10.imprint","IMPRINT",EDGE,{"derivedFrom":sQuery(id+"F10.wireOp",EDGE,"E287")}),1.0]])]});
            var Q3;
            Q3=sQuery(id+"F10.wireOp",EDGE,"E287");
            var Q4;
            Q4=sQuery(id+"F10.wireOp",EDGE,"E288");
            var Q5;
            Q5=sQuery(id+"F10.wireOp",EDGE,"E289");
            extrude(context, id + "F11", {"entities" : qUnion([Q0, Q1, Q2]), "operationType" : NewBodyOperationType.REMOVE, "surfaceEntities" : qUnion([Q3, Q4, Q5]), "oppositeDirection" : true, "depth" : 2.5 * mm, "offsetDistance" : 25 * mm});
        }
        {
            var Q0;
            Q0=makeQuery(id+"F0.imprint","IMPRINT",FACE,{"disambiguationData":[TD([[makeQuery(id+"F0.imprint","IMPRINT",EDGE,{"derivedFrom":sQuery(id+"F0.wireOp",EDGE,"E263")}),1.0]])]});
            var Q1;
            Q1=makeQuery(id+"F0.imprint","IMPRINT",FACE,{"disambiguationData":[TD([[makeQuery(id+"F0.imprint","IMPRINT",EDGE,{"derivedFrom":sQuery(id+"F0.wireOp",EDGE,"E255")}),-1.0]])]});
            extrude(context, id + "F12", {"entities" : qUnion([Q0, Q1]), "operationType" : NewBodyOperationType.REMOVE, "depth" : 5 * mm, "offsetDistance" : 25 * mm});
        }
        {
            var Q0;
            Q0=makeQuery(id+"F0.imprint","IMPRINT",FACE,{"disambiguationData":[TD([[makeQuery(id+"F0.imprint","IMPRINT",EDGE,{"derivedFrom":sQuery(id+"F0.wireOp",EDGE,"E32")}),-1.0]])]});
            extrude(context, id + "F13", {"entities" : qUnion([Q0]), "operationType" : NewBodyOperationType.REMOVE, "depth" : 1 * mm, "offsetDistance" : 25 * mm});
        }
    });
